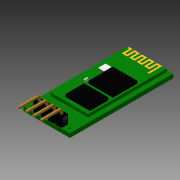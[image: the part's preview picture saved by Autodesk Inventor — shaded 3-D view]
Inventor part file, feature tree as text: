
AUTODESK INVENTOR PART (.ipt)
format: ipt  version: 2014 (Build 180170000, 170)  size: 360,448 bytes
history: native  units: in
note: dims shown in document units (in); Inventor stores cm internally (conversion verified against a paired STEP export)
features: extrude x10, sketch x10, plane x4, fillet x2, chamfer x2, pattern_linear x1, projected_geometry x1
ambient origin geometry x8: Origin, YZ Plane, XZ Plane, XY Plane, X Axis, Y Axis, Z Axis, Center Point
bodies: Solid1 (feature_tree)
feature tree (30):
  extrude  "Extrusion1"  Depth=1.4in
  extrude  "Extrusion2"  Depth=0.505in
  extrude  "Extrusion3"  Depth=0.0615in
  extrude  "Extrusion4"  Depth=0.03in
  extrude  "Extrusion5"  Depth=0.33in
  fillet  "Fillet1"  Radius=0.25in
  plane  "Work Plane1"
  extrude  "Extrusion6"  Depth=0.373in
  chamfer  "Chamfer1"  Distance=0.033in
  extrude  "Extrusion7"  Depth=0.044in
  chamfer  "Chamfer2"  Distance=0.033in
  fillet  "Fillet2"  Radius=0.097in
  pattern_linear  "Rectangular Pattern2"  Spacing1=0.004in  [1 undecoded]
  extrude  "Extrusion8"  Depth=0.115in
  extrude  "Extrusion9"  Depth=0.113in TaperAngle=0.0deg
  extrude  "Extrusion10"  Depth=0.02in
  sketch  "Sketch1"  dims[d0=0.628in d1=1.4in]
  sketch  "Sketch2"  dims[d2=0.055in d3=0.0in d4=0.505in]
  sketch  "Sketch3"  dims[d5=0.0615in d6=0.0615in]
  sketch  "Sketch4"  dims[d7=1.063in d8=0.03in]
  sketch  "Sketch5"  dims[d9=0.04in d10=0.0in d11=0.33in d12=0.25in]
  sketch  "Sketch6"  dims[d13=0.06in d14=0.373in]
  projected_geometry  "Projected Loop1"
  sketch  "Sketch7"  dims[d15=0.024in d16=0.033in d17=0.0in]
  plane  "Work Plane2"
  plane  "Work Plane3"
  plane  "Work Plane4"
  sketch  "Sketch8"  dims[d18=0.029in d19=0.044in]
  sketch  "Sketch9"  dims[d20=0.044in]
  sketch  "Sketch10"  dims[d21=0.044in d22=0.033in d23=0.0in d24=0.097in d25=0.004in d26=0.115in d27=0.113in d28=0.0in d29=0.02in d33=-0.03in d34=0.025in d35=0.025in d36=0.025in d37=0.075in d38=0.3in d39=0.03in d40=0.045in d41=0.025in d42=0.0in d43=0.01in d44=0.125in d45=45.0deg d46=0.02in d47=0.0in d48=0.01in d49=0.125in d50=45.0deg d51=0.01in d52=1.5748in d54=0.1in d55=0.053in d56=0.015in d57=0.039in d58=0.015in d59=0.03in d60=0.0in d61=0.025in d62=0.025in d63=0.025in d64=0.025in d65=0.025in d66=0.025in d67=0.025in d68=0.025in d69=0.025in d70=0.025in d71=0.025in d72=0.025in d73=0.025in d74=0.025in d75=0.025in d76=0.025in d77=0.025in d78=0.025in d79=0.025in d80=0.025in d81=0.055in d82=0.125in d83=0.004in d84=0.18in d85=0.004in d86=0.0in d87=0.1in d88=0.08in d89=0.02in d90=0.02in d91=0.0in]
note: 1 required parameter value undecoded (feature->parameter linkage not recoverable at this tier; creation-order binding heuristic only, values carry confidence <= 0.55)
